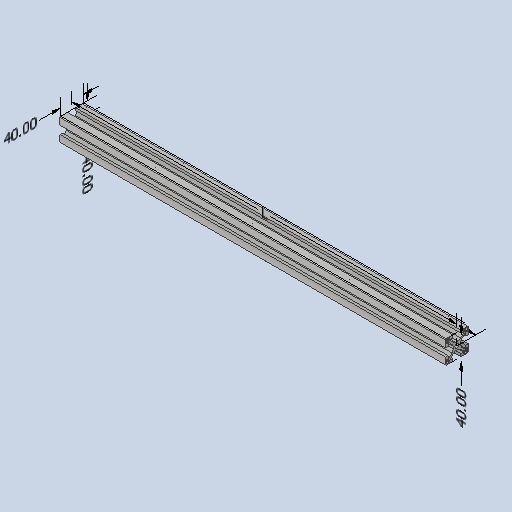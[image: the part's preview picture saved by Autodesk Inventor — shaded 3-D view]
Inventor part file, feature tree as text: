
AUTODESK INVENTOR PART (.ipt)
format: ipt  version: 2023 (Build 270158000, 158)  size: 274,432 bytes
history: native  units: mm
features: other x125, extrude x1, sketch x1
ambient origin geometry x8: Origin, YZ Plane, XZ Plane, XY Plane, X Axis, Y Axis, Z Axis, Center Point
bodies: Solid1 (feature_tree)
feature tree (127):
  other  "Annotations"
  extrude  "Extrusion1"  [1 undecoded]
  other  "CS_ANBAU_HINTEN_LINKS_XY"
  other  "CS_ANBAU_HINTEN_LINKS_YZ"
  other  "CS_ANBAU_HINTEN_LINKS_ZX"
  other  "CS_ANBAU_HINTEN_LINKS_X"
  other  "CS_ANBAU_HINTEN_LINKS_Y"
  other  "CS_ANBAU_HINTEN_LINKS_Z"
  other  "CS_ANBAU_HINTEN_LINKS_Center"
  other  "CS_ANBAU_HINTEN_OBEN_XY"
  other  "CS_ANBAU_HINTEN_OBEN_YZ"
  other  "CS_ANBAU_HINTEN_OBEN_ZX"
  other  "CS_ANBAU_HINTEN_OBEN_X"
  other  "CS_ANBAU_HINTEN_OBEN_Y"
  other  "CS_ANBAU_HINTEN_OBEN_Z"
  other  "CS_ANBAU_HINTEN_OBEN_Center"
  other  "CS_ANBAU_HINTEN_RECHTS_XY"
  other  "CS_ANBAU_HINTEN_RECHTS_YZ"
  other  "CS_ANBAU_HINTEN_RECHTS_ZX"
  other  "CS_ANBAU_HINTEN_RECHTS_X"
  other  "CS_ANBAU_HINTEN_RECHTS_Y"
  other  "CS_ANBAU_HINTEN_RECHTS_Z"
  other  "CS_ANBAU_HINTEN_RECHTS_Center"
  other  "CS_ANBAU_HINTEN_UNTEN_XY"
  other  "CS_ANBAU_HINTEN_UNTEN_YZ"
  other  "CS_ANBAU_HINTEN_UNTEN_ZX"
  other  "CS_ANBAU_HINTEN_UNTEN_X"
  other  "CS_ANBAU_HINTEN_UNTEN_Y"
  other  "CS_ANBAU_HINTEN_UNTEN_Z"
  other  "CS_ANBAU_HINTEN_UNTEN_Center"
  other  "CS_ANBAU_QUER_XY"
  other  "CS_ANBAU_QUER_YZ"
  other  "CS_ANBAU_QUER_ZX"
  other  "CS_ANBAU_QUER_X"
  other  "CS_ANBAU_QUER_Y"
  other  "CS_ANBAU_QUER_Z"
  other  "CS_ANBAU_QUER_Center"
  other  "CS_ANBAU_QUER_1_XY"
  other  "CS_ANBAU_QUER_1_YZ"
  other  "CS_ANBAU_QUER_1_ZX"
  other  "CS_ANBAU_QUER_1_X"
  other  "CS_ANBAU_QUER_1_Y"
  other  "CS_ANBAU_QUER_1_Z"
  other  "CS_ANBAU_QUER_1_Center"
  other  "CS_ANBAU_VORNE_LINKS_XY"
  other  "CS_ANBAU_VORNE_LINKS_YZ"
  other  "CS_ANBAU_VORNE_LINKS_ZX"
  other  "CS_ANBAU_VORNE_LINKS_X"
  other  "CS_ANBAU_VORNE_LINKS_Y"
  other  "CS_ANBAU_VORNE_LINKS_Z"
  other  "CS_ANBAU_VORNE_LINKS_Center"
  other  "CS_ANBAU_VORNE_OBEN_XY"
  other  "CS_ANBAU_VORNE_OBEN_YZ"
  other  "CS_ANBAU_VORNE_OBEN_ZX"
  other  "CS_ANBAU_VORNE_OBEN_X"
  other  "CS_ANBAU_VORNE_OBEN_Y"
  other  "CS_ANBAU_VORNE_OBEN_Z"
  other  "CS_ANBAU_VORNE_OBEN_Center"
  other  "CS_ANBAU_VORNE_RECHTS_XY"
  other  "CS_ANBAU_VORNE_RECHTS_YZ"
  other  "CS_ANBAU_VORNE_RECHTS_ZX"
  other  "CS_ANBAU_VORNE_RECHTS_X"
  other  "CS_ANBAU_VORNE_RECHTS_Y"
  other  "CS_ANBAU_VORNE_RECHTS_Z"
  other  "CS_ANBAU_VORNE_RECHTS_Center"
  other  "CS_ANBAU_VORNE_UNTEN_XY"
  other  "CS_ANBAU_VORNE_UNTEN_YZ"
  other  "CS_ANBAU_VORNE_UNTEN_ZX"
  other  "CS_ANBAU_VORNE_UNTEN_X"
  other  "CS_ANBAU_VORNE_UNTEN_Y"
  other  "CS_ANBAU_VORNE_UNTEN_Z"
  other  "CS_ANBAU_VORNE_UNTEN_Center"
  other  "p1_XY"
  other  "p1_YZ"
  other  "p1_ZX"
  other  "p1_X"
  other  "p1_Y"
  other  "p1_Z"
  other  "p1_Center"
  other  "p2_XY"
  other  "p2_YZ"
  other  "p2_ZX"
  other  "p2_X"
  other  "p2_Y"
  other  "p2_Z"
  other  "p2_Center"
  other  "p3_XY"
  other  "p3_YZ"
  other  "p3_ZX"
  other  "p3_X"
  other  "p3_Y"
  other  "p3_Z"
  other  "p3_Center"
  other  "p4_XY"
  other  "p4_YZ"
  other  "p4_ZX"
  other  "p4_X"
  other  "p4_Y"
  other  "p4_Z"
  other  "p4_Center"
  other  "p5_XY"
  other  "p5_YZ"
  other  "p5_ZX"
  other  "p5_X"
  other  "p5_Y"
  other  "p5_Z"
  other  "p5_Center"
  other  "pm1_XY"
  other  "pm1_YZ"
  other  "pm1_ZX"
  other  "pm1_X"
  other  "pm1_Y"
  other  "pm1_Z"
  other  "pm1_Center"
  other  "pm2_XY"
  other  "pm2_YZ"
  other  "pm2_ZX"
  other  "pm2_X"
  other  "pm2_Y"
  other  "pm2_Z"
  other  "pm2_Center"
  sketch  "Skizze_1"  dims[d0=670.0mm d1=0.0mm d2=0.0mm d3=0.0mm d4=0.0mm d5=0.0mm d6=0.0mm d10=670.0mm d11=670.0mm d7=40.0mm d8=40.0mm d9=40.0mm]
  other  "Linear Dimension 1"
  other  "Linear Dimension 2"
  other  "Linear Dimension 3"
  other  "Linear Dimension 4"
  other  "Linear Dimension 5"
note: 1 required parameter value undecoded (feature->parameter linkage not recoverable at this tier; creation-order binding heuristic only, values carry confidence <= 0.55)
